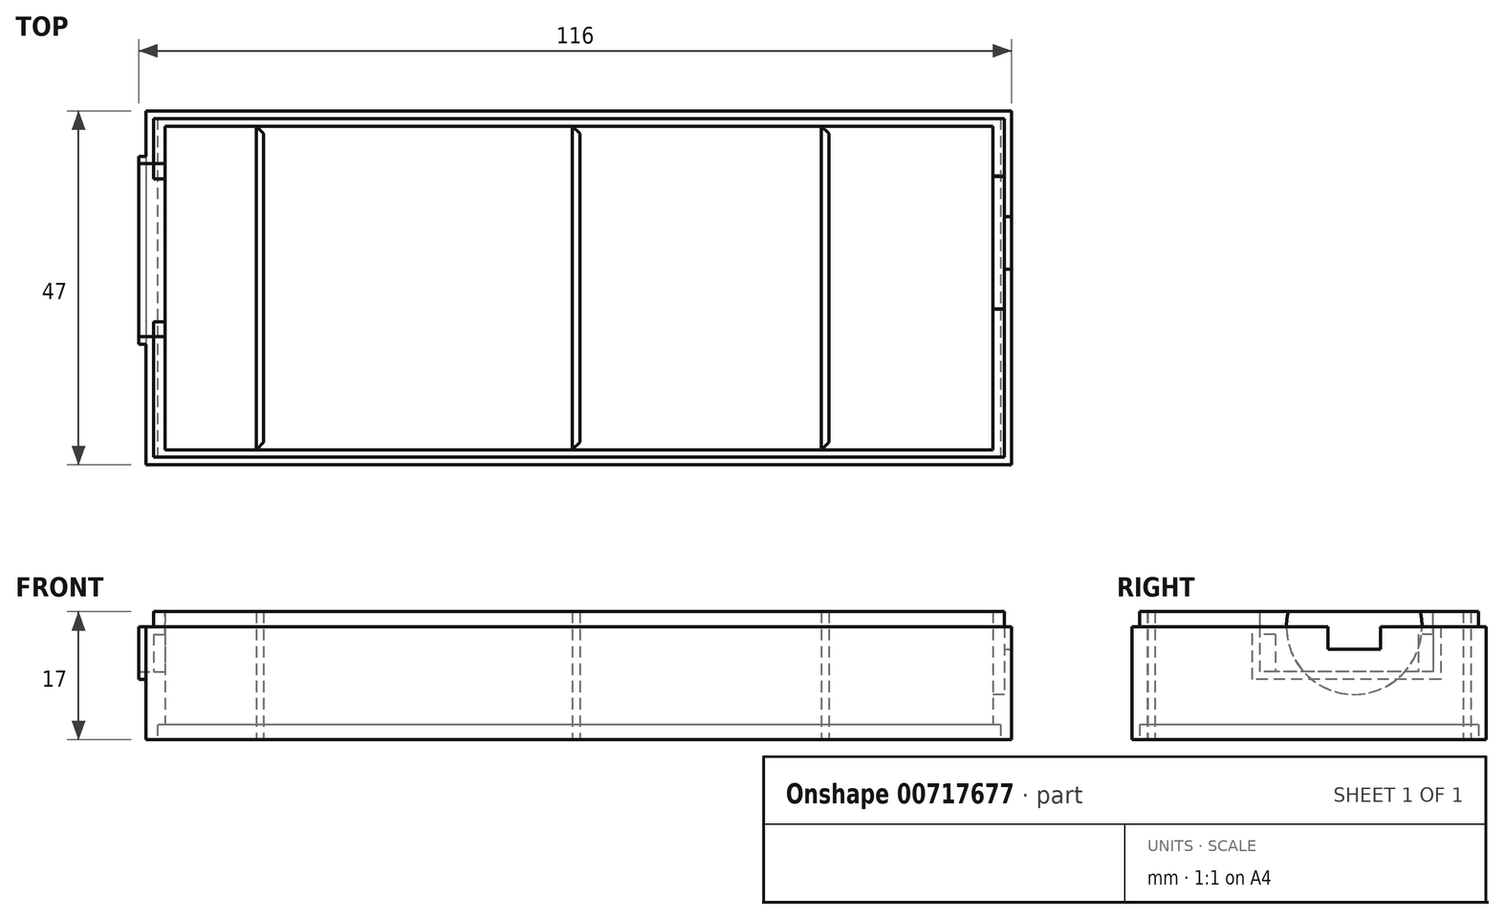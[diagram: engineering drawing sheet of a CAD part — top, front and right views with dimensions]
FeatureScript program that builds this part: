
annotation { "Feature Type Name" : "Feature", "Feature Type Description" : "" }
export const myFeature = defineFeature(function(context is Context, id is Id, definition is map)
    precondition{}
    {
        {
            var Q0;
            Q0=qCreatedBy(makeId("Top.planeOp"),FACE);
            var sketch = newSketch(context, id + "F0", { "sketchPlane" : qUnion([Q0])});
            skLineSegment(sketch, "E0.bottom", {"start": v(57.5, 23.5) * mm, "end": v(-57.5, 23.5) * mm});
            skLineSegment(sketch, "E0.top", {"start": v(57.5, -23.5) * mm, "end": v(-57.5, -23.5) * mm});
            skLineSegment(sketch, "E0.left", {"start": v(57.5, 23.5) * mm, "end": v(57.5, -23.5) * mm});
            skLineSegment(sketch, "E0.right", {"start": v(-57.5, 23.5) * mm, "end": v(-57.5, -23.5) * mm});
            skLineSegment(sketch, "E1.bottom", {"start": v(56, 22.5) * mm, "end": v(-56, 22.5) * mm});
            skLineSegment(sketch, "E1.top", {"start": v(56, -22.5) * mm, "end": v(-56, -22.5) * mm});
            skLineSegment(sketch, "E1.left", {"start": v(56, 22.5) * mm, "end": v(56, -22.5) * mm});
            skLineSegment(sketch, "E1.right", {"start": v(-56, 22.5) * mm, "end": v(-56, -22.5) * mm});
            skSolve(sketch);
        }
        {
            var Q0;
            Q0=makeQuery(id+"F0.imprint","IMPRINT",FACE,{"disambiguationData":[TD([[makeQuery(id+"F0.imprint","IMPRINT",EDGE,{"derivedFrom":sQuery(id+"F0.wireOp",EDGE,"E0.bottom")}),1.0]])]});
            extrude(context, id + "F1", {"entities" : qUnion([Q0]), "depth" : 15 * mm, "offsetDistance" : 25 * mm});
        }
        {
            var Q0;
            Q0=qCreatedBy(makeId("Top.planeOp"),FACE);
            cPlane(context, id + "F2", {"entities" : qUnion([Q0]), "cplaneType" : CPlaneType.OFFSET, "offset" : 2 * mm, "width" : 150 * mm, "height" : 150 * mm});
        }
        {
            var Q0;
            Q0=qCreatedBy(id+"F2.planeOp",FACE);
            var sketch = newSketch(context, id + "F3", { "sketchPlane" : qUnion([Q0])});
            skLineSegment(sketch, "E2.bottom", {"start": v(56.5, 22.5) * mm, "end": v(-56.5, 22.5) * mm});
            skLineSegment(sketch, "E2.top", {"start": v(56.5, -22.5) * mm, "end": v(-56.5, -22.5) * mm});
            skLineSegment(sketch, "E2.left", {"start": v(56.5, 22.5) * mm, "end": v(56.5, -22.5) * mm});
            skLineSegment(sketch, "E2.right", {"start": v(-56.5, 22.5) * mm, "end": v(-56.5, -22.5) * mm});
            skLineSegment(sketch, "E3.bottom", {"start": v(55, 21.5) * mm, "end": v(-55, 21.5) * mm});
            skLineSegment(sketch, "E3.top", {"start": v(55, -21.5) * mm, "end": v(-55, -21.5) * mm});
            skLineSegment(sketch, "E3.left", {"start": v(55, 21.5) * mm, "end": v(55, -21.5) * mm});
            skLineSegment(sketch, "E3.right", {"start": v(-55, 21.5) * mm, "end": v(-55, -21.5) * mm});
            skSolve(sketch);
        }
        {
            var Q0;
            Q0 = qSketchRegion(id + "F3", true);
            extrude(context, id + "F4", {"entities" : qUnion([Q0]), "operationType" : NewBodyOperationType.ADD, "depth" : 15 * mm, "offsetDistance" : 25 * mm});
        }
        {
            var Q0;
            Q0=makeQuery(id+"F1.opExtrude","SWEPT_FACE",FACE,{"disambiguationData":[OSD([sQuery(id+"F0.wireOp",EDGE,"E0.left")])]});
            var sketch = newSketch(context, id + "F5", { "sketchPlane" : qUnion([Q0])});
            skLineSegment(sketch, "E4.bottom", {"start": v(9.5, 17) * mm, "end": v(2.5, 17) * mm});
            skLineSegment(sketch, "E4.top", {"start": v(9.5, 12) * mm, "end": v(2.5, 12) * mm});
            skLineSegment(sketch, "E4.left", {"start": v(9.5, 17) * mm, "end": v(9.5, 12) * mm});
            skLineSegment(sketch, "E4.right", {"start": v(2.5, 17) * mm, "end": v(2.5, 12) * mm});
            skSolve(sketch);
        }
        {
            var Q0;
            {var subQ0=sQuery(id+"F5.wireOp",EDGE,"E4.bottom");Q0=makeQuery(id+"F5.imprint","IMPRINT",FACE,{"disambiguationData":[TD([[makeQuery(id+"F5.imprint","IMPRINT",EDGE,{"derivedFrom":subQ0}),1.0]])]});}
            var Q1;
            {var subQ0=sQuery(id+"F5.wireOp",EDGE,"E4.top");Q1=makeQuery(id+"F5.imprint","IMPRINT",FACE,{"disambiguationData":[TD([[makeQuery(id+"F5.imprint","IMPRINT",EDGE,{"derivedFrom":subQ0}),-1.0]])]});}
            extrude(context, id + "F6", {"entities" : qUnion([Q0, Q1]), "operationType" : NewBodyOperationType.REMOVE, "oppositeDirection" : true, "depth" : 25 * mm, "offsetDistance" : 25 * mm});
        }
        {
            var Q0;
            Q0=makeQuery(id+"F4.opExtrude","SWEPT_FACE",FACE,{"disambiguationData":[OSD([sQuery(id+"F3.wireOp",EDGE,"E3.left")])]});
            var sketch = newSketch(context, id + "F7", { "sketchPlane" : qUnion([Q0])});
            skCircle(sketch, "E5", {"center": v(-6, 15) * mm, "radius": 9 * mm});
            skSolve(sketch);
        }
        {
            var Q0;
            {var subQ1=sQuery(id+"F3.wireOp",EDGE,"E3.left");var subQ2=makeQuery(id+"F4.opExtrude","SWEPT_FACE",FACE,{"disambiguationData":[OSD([subQ1])]});Q0=makeQuery(id+"F7.imprint","IMPRINT",FACE,{"disambiguationData":[TD([[makeQuery(id+"F7.imprint","IMPRINT",EDGE,{"derivedFrom":makeQuery(id+"F6.boolean.opBoolean","INTERSECT",EDGE,{"derivedFrom":[subQ2,makeQuery(id+"F6.opExtrude","SWEPT_FACE",FACE,{"disambiguationData":[OSD([sQuery(id+"F5.wireOp",EDGE,"E4.top")])]})]})}),1.0]])]});}
            var Q1;
            {var subQ1=sQuery(id+"F3.wireOp",EDGE,"E3.left");var subQ2=makeQuery(id+"F4.opExtrude","SWEPT_FACE",FACE,{"disambiguationData":[OSD([subQ1])]});Q1=makeQuery(id+"F7.imprint","IMPRINT",FACE,{"disambiguationData":[TD([[makeQuery(id+"F7.imprint","IMPRINT",EDGE,{"derivedFrom":makeQuery(id+"F6.boolean.opBoolean","INTERSECT",EDGE,{"derivedFrom":[subQ2,makeQuery(id+"F6.opExtrude","SWEPT_FACE",FACE,{"disambiguationData":[OSD([sQuery(id+"F5.wireOp",EDGE,"E4.top")])]})]})}),-1.0]])]});}
            var Q2;
            Q2=sQuery(id+"F7.wireOp",EDGE,"E5");
            extrude(context, id + "F8", {"entities" : qUnion([Q0, Q1]), "operationType" : NewBodyOperationType.REMOVE, "surfaceEntities" : qUnion([Q2]), "oppositeDirection" : true, "depth" : 1.5 * mm, "offsetDistance" : 25 * mm});
        }
        {
            var Q0;
            Q0=makeQuery(id+"F4.opExtrude","SWEPT_FACE",FACE,{"disambiguationData":[OSD([sQuery(id+"F3.wireOp",EDGE,"E3.right")])]});
            var sketch = newSketch(context, id + "F9", { "sketchPlane" : qUnion([Q0])});
            skLineSegment(sketch, "E6.bottom", {"start": v(14.5, 17) * mm, "end": v(-4.5, 17) * mm});
            skLineSegment(sketch, "E6.top", {"start": v(14.5, 9) * mm, "end": v(-4.5, 9) * mm});
            skLineSegment(sketch, "E6.left", {"start": v(14.5, 17) * mm, "end": v(14.5, 9) * mm});
            skLineSegment(sketch, "E6.right", {"start": v(-4.5, 17) * mm, "end": v(-4.5, 9) * mm});
            skLineSegment(sketch, "E7.bottom", {"start": v(16.5, 14) * mm, "end": v(-6.5, 14) * mm});
            skLineSegment(sketch, "E7.top", {"start": v(16.5, 17) * mm, "end": v(-6.5, 17) * mm});
            skLineSegment(sketch, "E7.left", {"start": v(16.5, 14) * mm, "end": v(16.5, 17) * mm});
            skLineSegment(sketch, "E7.right", {"start": v(-6.5, 14) * mm, "end": v(-6.5, 17) * mm});
            skSolve(sketch);
        }
        {
            var Q0;
            {var subQ5=sQuery(id+"F9.wireOp",EDGE,"E7.right");Q0=makeQuery(id+"F9.imprint","IMPRINT",FACE,{"disambiguationData":[TD([[makeQuery(id+"F9.imprint","IMPRINT",EDGE,{"derivedFrom":subQ5}),-1.0]])]});}
            var Q1;
            {var subQ0=sQuery(id+"F9.wireOp",EDGE,"E6.top");Q1=makeQuery(id+"F9.imprint","IMPRINT",FACE,{"disambiguationData":[TD([[makeQuery(id+"F9.imprint","IMPRINT",EDGE,{"derivedFrom":subQ0}),-1.0]])]});}
            var Q2;
            {var subQ5=sQuery(id+"F9.wireOp",EDGE,"E7.left");Q2=makeQuery(id+"F9.imprint","IMPRINT",FACE,{"disambiguationData":[TD([[makeQuery(id+"F9.imprint","IMPRINT",EDGE,{"derivedFrom":subQ5}),1.0]])]});}
            var Q3;
            {var subQ0=sQuery(id+"F9.wireOp",EDGE,"E7.top");var subQ1=sQuery(id+"F9.wireOp",EDGE,"E6.left");var subQ2=makeQuery(id+"F9.imprint","INTERSECT",VERTEX,{"derivedFrom":[subQ1,subQ0]});Q3=makeQuery(id+"F9.imprint","IMPRINT",FACE,{"disambiguationData":[TD([[makeQuery(id+"F9.imprint","IMPRINT",EDGE,{"disambiguationData":[TD([[subQ2,-1.0]])],"derivedFrom":subQ1}),-1.0]])]});}
            extrude(context, id + "F10", {"entities" : qUnion([Q0, Q1, Q2, Q3]), "operationType" : NewBodyOperationType.REMOVE, "oppositeDirection" : true, "depth" : 25 * mm, "offsetDistance" : 25 * mm});
        }
        {
            var Q0;
            Q0=makeQuery(id+"F1.opExtrude","SWEPT_FACE",FACE,{"disambiguationData":[OSD([sQuery(id+"F0.wireOp",EDGE,"E0.right")])]});
            var sketch = newSketch(context, id + "F11", { "sketchPlane" : qUnion([Q0])});
            skLineSegment(sketch, "E8", {"start": v(-17.5, 15) * mm, "end": v(-17.5, 8) * mm});
            skLineSegment(sketch, "E9", {"start": v(-17.5, 8) * mm, "end": v(7.5, 8) * mm});
            skLineSegment(sketch, "E10", {"start": v(7.5, 8) * mm, "end": v(7.5, 15) * mm});
            skLineSegment(sketch, "E11", {"start": v(-16.5, 14) * mm, "end": v(-16.5, 9) * mm});
            skLineSegment(sketch, "E12", {"start": v(-16.5, 9) * mm, "end": v(6.5, 9) * mm});
            skLineSegment(sketch, "E13", {"start": v(6.5, 9) * mm, "end": v(6.5, 14) * mm});
            skSolve(sketch);
        }
        {
            var Q0;
            {var subQ11=sQuery(id+"F11.wireOp",EDGE,"E8");Q0=makeQuery(id+"F11.imprint","IMPRINT",FACE,{"disambiguationData":[TD([[makeQuery(id+"F11.imprint","IMPRINT",EDGE,{"derivedFrom":subQ11}),1.0]])]});}
            extrude(context, id + "F12", {"entities" : qUnion([Q0]), "operationType" : NewBodyOperationType.ADD, "depth" : 1 * mm, "offsetDistance" : 25 * mm});
        }
        {
            var Q0;
            {var subQ2=sQuery(id+"F9.wireOp",EDGE,"E6.left");var subQ3=sQuery(id+"F0.wireOp",EDGE,"E0.right");Q0=makeQuery(id+"F12.boolean.opBoolean","SPLIT",FACE,{"disambiguationData":[TD([makeQuery(id+"F10.boolean.opBoolean","COPY",FACE,{"derivedFrom":makeQuery(id+"F10.opExtrude","SWEPT_FACE",FACE,{"disambiguationData":[OSD([subQ2])]})})])],"derivedFrom":makeQuery(id+"F1.opExtrude","SWEPT_FACE",FACE,{"disambiguationData":[OSD([subQ3])]})});}
            var Q1;
            {var subQ2=sQuery(id+"F9.wireOp",EDGE,"E6.right");var subQ3=sQuery(id+"F0.wireOp",EDGE,"E0.right");Q1=makeQuery(id+"F12.boolean.opBoolean","SPLIT",FACE,{"disambiguationData":[TD([makeQuery(id+"F10.boolean.opBoolean","COPY",FACE,{"derivedFrom":makeQuery(id+"F10.opExtrude","SWEPT_FACE",FACE,{"disambiguationData":[OSD([subQ2])]})})])],"derivedFrom":makeQuery(id+"F1.opExtrude","SWEPT_FACE",FACE,{"disambiguationData":[OSD([subQ3])]})});}
            extrude(context, id + "F13", {"entities" : qUnion([Q0, Q1]), "operationType" : NewBodyOperationType.REMOVE, "oppositeDirection" : true, "depth" : 1 * mm, "offsetDistance" : 25 * mm});
        }
        {
            var Q0;
            Q0=qCreatedBy(makeId("Top.planeOp"),FACE);
            var sketch = newSketch(context, id + "F14", { "sketchPlane" : qUnion([Q0])});
            skLineSegment(sketch, "E14", {"start": v(-42.88, 21.5) * mm, "end": v(-42.88, -21.5) * mm});
            skLineSegment(sketch, "E15", {"start": v(-41.88, -20.5) * mm, "end": v(-42.88, -21.5) * mm});
            skLineSegment(sketch, "E16", {"start": v(-41.88, -20.5) * mm, "end": v(-41.88, 20.5) * mm});
            skLineSegment(sketch, "E17", {"start": v(-41.88, 20.5) * mm, "end": v(-42.88, 21.5) * mm});
            skLineSegment(sketch, "E18", {"start": v(-0.86, 21.5) * mm, "end": v(-0.86, -21.45) * mm});
            skLineSegment(sketch, "E19", {"start": v(0.14, -20.5) * mm, "end": v(-0.86, -21.45) * mm});
            skLineSegment(sketch, "E20", {"start": v(0.14, -20.5) * mm, "end": v(0.14, 20.5) * mm});
            skLineSegment(sketch, "E21", {"start": v(0.14, 20.5) * mm, "end": v(-0.86, 21.5) * mm});
            skLineSegment(sketch, "E22", {"start": v(32.21, 21.5) * mm, "end": v(32.21, -21.5) * mm});
            skLineSegment(sketch, "E23", {"start": v(33.21, -20.5) * mm, "end": v(32.21, -21.5) * mm});
            skLineSegment(sketch, "E24", {"start": v(33.21, -20.5) * mm, "end": v(33.21, 20.5) * mm});
            skLineSegment(sketch, "E25", {"start": v(33.21, 20.5) * mm, "end": v(32.21, 21.5) * mm});
            skSolve(sketch);
        }
        {
            var Q0;
            Q0 = qSketchRegion(id + "F14", true);
            extrude(context, id + "F15", {"entities" : qUnion([Q0]), "depth" : 17 * mm, "offsetDistance" : 25 * mm});
        }
    });
